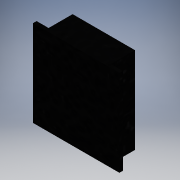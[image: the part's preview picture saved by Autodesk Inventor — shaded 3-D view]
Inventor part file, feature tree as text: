
AUTODESK INVENTOR PART (.ipt)
format: ipt  version: 2016 (Build 200138000, 138)  size: 127,488 bytes
history: native  units: mm
features: reference x9, sketch x4, extrude x2, hole x2
ambient origin geometry x8: Origin, YZ Plane, XZ Plane, XY Plane, X Axis, Y Axis, Z Axis, Center Point
bodies: Solid1 (feature_tree)
feature tree (17):
  extrude  "Extrusion1"  Depth=72.0mm
  extrude  "Extrusion2"  Depth=52.0mm
  hole  "Hole2"  [1 undecoded]
  hole  "Hole4"  [1 undecoded]
  sketch  "Sketch1"  dims[d0=72.0mm d1=72.0mm]
  sketch  "Sketch2"  dims[d2=3.0mm d3=0.0mm d4=52.0mm]
  sketch  "Sketch3"  dims[d5=20.0mm d6=0.0mm d7=4.0mm]
  reference  "Reference1"
  reference  "Reference2"
  reference  "Reference3"
  reference  "Reference4"
  sketch  "Sketch4"  dims[d8=4.0mm d16=4.0mm d17=6.0mm d18=4.0mm d19=2.0mm d20=90.0deg d21=8.0mm d22=20.594885mm d30=4.0mm d31=6.0mm d32=4.0mm d33=2.0mm d34=90.0deg d35=8.0mm d36=20.594885mm]
  reference  "Reference5"
  reference  "Reference6"
  reference  "Reference7"
  reference  "Reference8"
  reference  "Reference9"
note: 2 required parameter values undecoded (feature->parameter linkage not recoverable at this tier; creation-order binding heuristic only, values carry confidence <= 0.55)
